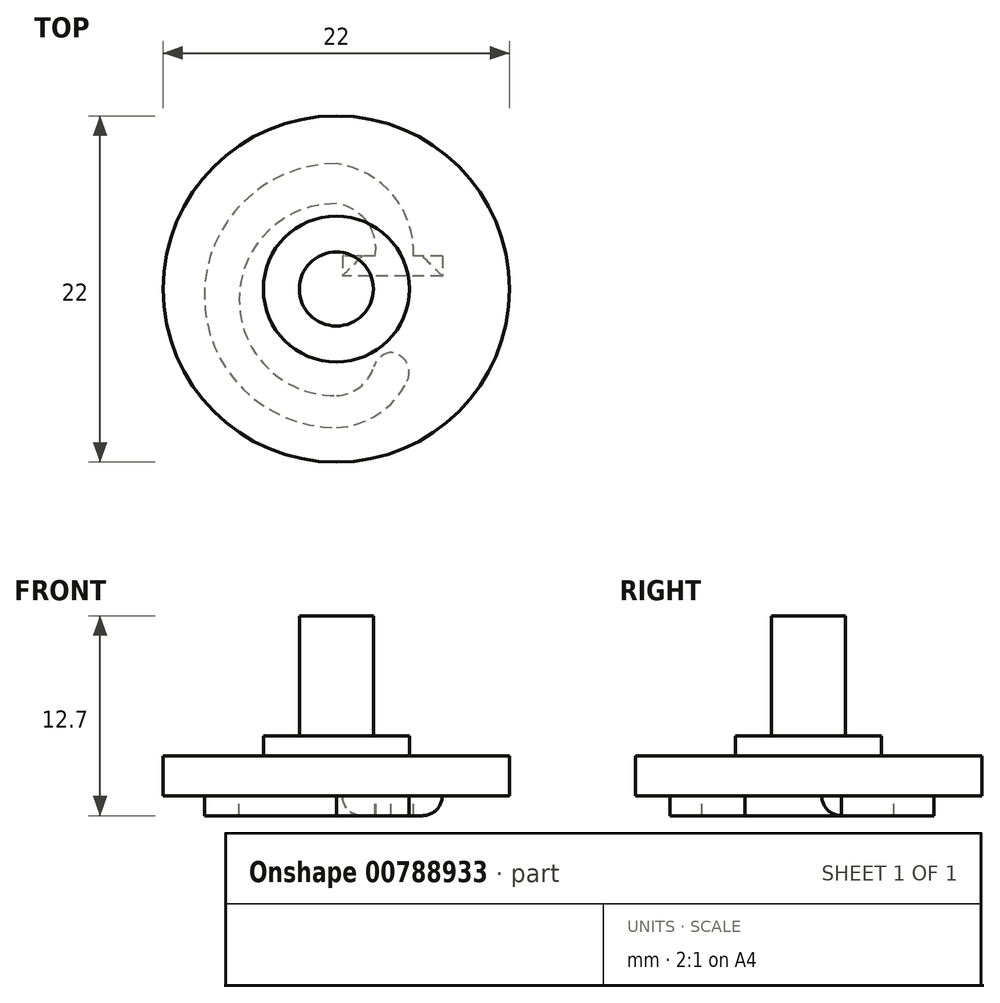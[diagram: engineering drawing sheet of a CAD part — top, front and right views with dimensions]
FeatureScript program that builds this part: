
annotation { "Feature Type Name" : "Feature", "Feature Type Description" : "" }
export const myFeature = defineFeature(function(context is Context, id is Id, definition is map)
    precondition{}
    {
        {
            var Q0;
            Q0=qCreatedBy(makeId("Top.planeOp"),FACE);
            var sketch = newSketch(context, id + "F0", { "sketchPlane" : qUnion([Q0])});
            skCircle(sketch, "E0", {"center": v(0, 0) * mm, "radius": 11 * mm});
            skCircle(sketch, "E1", {"center": v(0, 0) * mm, "radius": 4.64 * mm});
            skCircle(sketch, "E2", {"center": v(0, 0) * mm, "radius": 2.35 * mm});
            skSolve(sketch);
        }
        {
            var Q0;
            Q0=makeQuery(id+"F0.imprint","IMPRINT",FACE,{"disambiguationData":[TD([[makeQuery(id+"F0.imprint","IMPRINT",EDGE,{"derivedFrom":sQuery(id+"F0.wireOp",EDGE,"E2")}),1.0]])]});
            extrude(context, id + "F1", {"entities" : qUnion([Q0]), "depth" : 11.43 * mm, "offsetDistance" : 25.4 * mm});
        }
        {
            var Q0;
            Q0=makeQuery(id+"F0.imprint","IMPRINT",FACE,{"disambiguationData":[TD([[makeQuery(id+"F0.imprint","IMPRINT",EDGE,{"derivedFrom":sQuery(id+"F0.wireOp",EDGE,"E1")}),1.0]])]});
            extrude(context, id + "F2", {"entities" : qUnion([Q0]), "operationType" : NewBodyOperationType.ADD, "depth" : 3.8 * mm, "offsetDistance" : 25.4 * mm});
        }
        {
            var Q0;
            Q0=makeQuery(id+"F0.imprint","IMPRINT",FACE,{"disambiguationData":[TD([[makeQuery(id+"F0.imprint","IMPRINT",EDGE,{"derivedFrom":sQuery(id+"F0.wireOp",EDGE,"E0")}),1.0]])]});
            extrude(context, id + "F3", {"entities" : qUnion([Q0]), "operationType" : NewBodyOperationType.ADD, "depth" : 2.54 * mm, "offsetDistance" : 25.4 * mm});
        }
        {
            var Q0;
            Q0=makeQuery(id+"F0.imprint","IMPRINT",FACE,{"disambiguationData":[TD([[makeQuery(id+"F0.imprint","IMPRINT",EDGE,{"derivedFrom":sQuery(id+"F0.wireOp",EDGE,"E0")}),1.0]])]});
            var sketch = newSketch(context, id + "F4", { "sketchPlane" : qUnion([Q0])});
            skArc(sketch, "E3", {"start": v(0, 5.42) * mm, "mid": v(-6.17, -0.68) * mm, "end": v(0, -6.77) * mm});
            skArc(sketch, "E4", {"start": v(0, 7.96) * mm, "mid": v(-8.38, -0.42) * mm, "end": v(0, -8.8) * mm});
            skArc(sketch, "E5", {"start": v(4.83, 1.46) * mm, "mid": v(3.79, 5.73) * mm, "end": v(0, 7.96) * mm});
            skArc(sketch, "E6", {"start": v(2.29, 1.46) * mm, "mid": v(2.12, 4) * mm, "end": v(0, 5.42) * mm});
            skLineSegment(sketch, "E7", {"start": v(2.29, 1.46) * mm, "end": v(4.83, 1.46) * mm});
            skArc(sketch, "E8", {"start": v(0, -6.77) * mm, "mid": v(1.82, -5.93) * mm, "end": v(2.47, -4.03) * mm});
            skArc(sketch, "E9", {"start": v(0, -8.8) * mm, "mid": v(3.4, -7.35) * mm, "end": v(5.01, -4.03) * mm});
            skLineSegment(sketch, "E10", {"start": v(2.47, -4.03) * mm, "end": v(5.01, -4.03) * mm});
            skLineSegment(sketch, "E11.bottom", {"start": v(6.73, 2.1) * mm, "end": v(0.38, 2.1) * mm});
            skLineSegment(sketch, "E11.top", {"start": v(6.73, 0.83) * mm, "end": v(0.38, 0.83) * mm});
            skLineSegment(sketch, "E11.left", {"start": v(6.73, 2.1) * mm, "end": v(6.73, 0.83) * mm});
            skLineSegment(sketch, "E11.right", {"start": v(0.38, 2.1) * mm, "end": v(0.38, 0.83) * mm});
            skPoint(sketch, "E11.middle", {"position": v(3.56, 1.46) * mm});
            skSolve(sketch);
        }
        {
            var Q0;
            Q0 = qSketchRegion(id + "F4", true);
            extrude(context, id + "F5", {"entities" : qUnion([Q0]), "operationType" : NewBodyOperationType.ADD, "oppositeDirection" : true, "depth" : 1.27 * mm, "offsetDistance" : 25.4 * mm});
        }
        {
            var Q0;
            Q0=makeQuery(id+"F5.opExtrude","CAP_EDGE",EDGE,{"disambiguationData":[OSD([sQuery(id+"F4.wireOp",EDGE,"E11.top")])],"isStart":false});
            var Q1;
            Q1=makeQuery(id+"F5.opExtrude","CAP_EDGE",EDGE,{"disambiguationData":[OSD([sQuery(id+"F4.wireOp",EDGE,"E11.left")])],"isStart":false});
            var Q2;
            Q2=makeQuery(id+"F5.opExtrude","CAP_EDGE",EDGE,{"disambiguationData":[OSD([sQuery(id+"F4.wireOp",EDGE,"E11.right")])],"isStart":false});
            var Q3;
            Q3=makeQuery(id+"F5.opExtrude","SWEPT_EDGE",EDGE,{"disambiguationData":[OSD([sQuery(id+"F4.wireOp",EDGE,"E8"),sQuery(id+"F4.wireOp",EDGE,"E10")])]});
            var Q4;
            Q4=makeQuery(id+"F5.opExtrude","SWEPT_EDGE",EDGE,{"disambiguationData":[OSD([sQuery(id+"F4.wireOp",EDGE,"E9"),sQuery(id+"F4.wireOp",EDGE,"E10")])]});
            fillet(context, id + "F6", {"entities" : qUnion([Q0, Q1, Q2, Q3, Q4]), "radius" : 1.27 * mm, "tangentPropagation" : true, "allowEdgeOverflow" : false});
        }
    });
